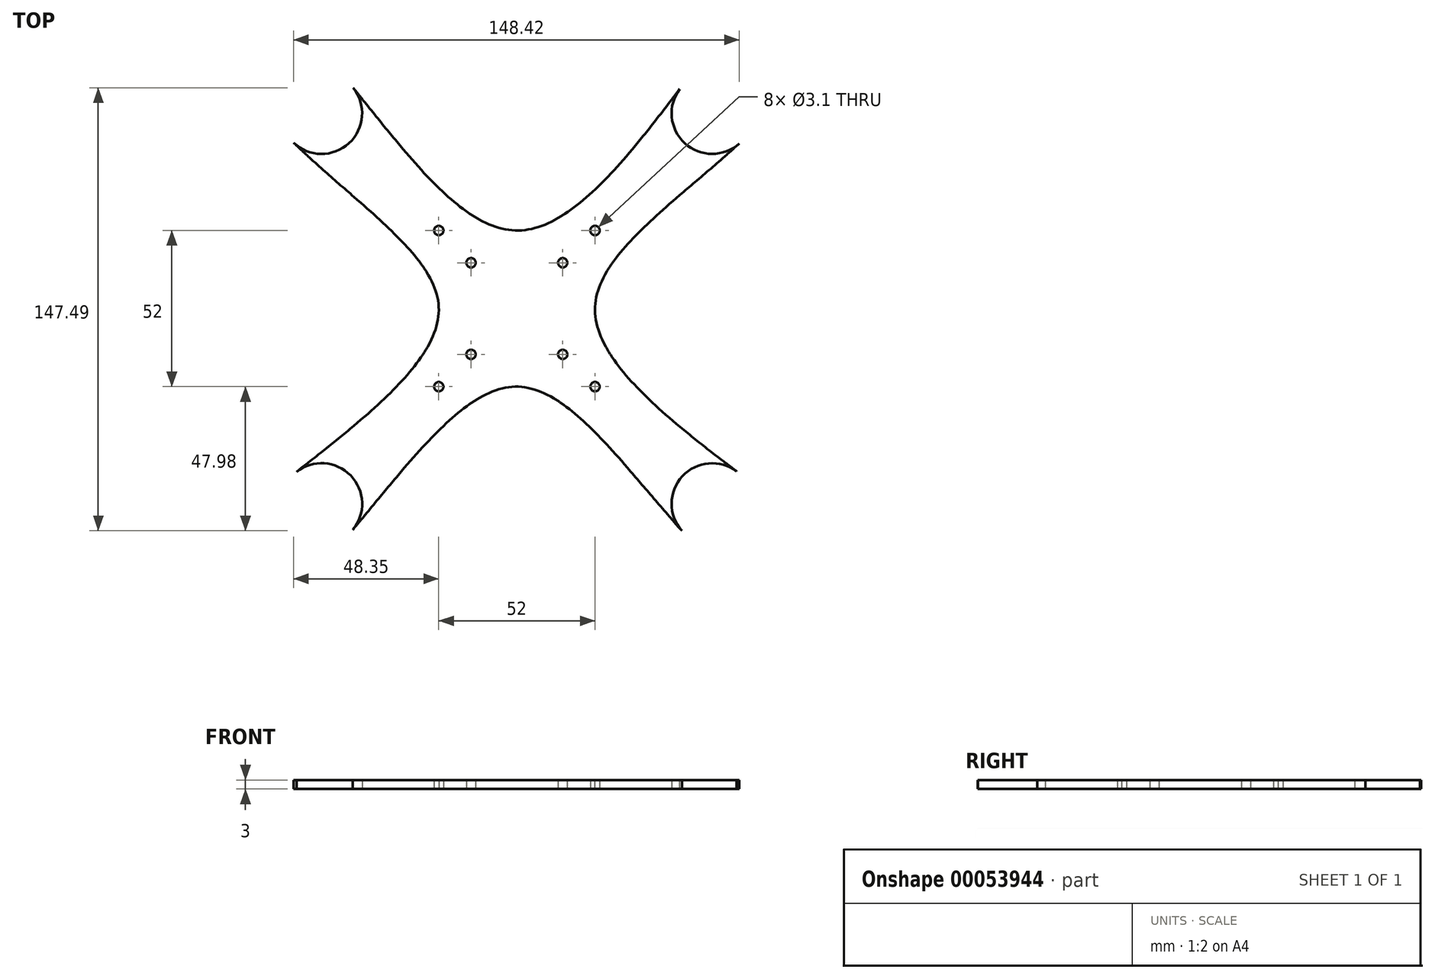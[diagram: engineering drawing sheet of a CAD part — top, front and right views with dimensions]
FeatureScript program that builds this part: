
annotation { "Feature Type Name" : "Feature", "Feature Type Description" : "" }
export const myFeature = defineFeature(function(context is Context, id is Id, definition is map)
    precondition{}
    {
        {
            var Q0;
            Q0=qCreatedBy(makeId("Top.planeOp"),FACE);
            var sketch = newSketch(context, id + "F0", { "sketchPlane" : qUnion([Q0])});
            skLineSegment(sketch, "E0.rect.bottom", {"start": v(-65, -65) * mm, "end": v(65, -65) * mm, "construction": true});
            skLineSegment(sketch, "E0.rect.top", {"start": v(-65, 65) * mm, "end": v(65, 65) * mm, "construction": true});
            skLineSegment(sketch, "E0.rect.left", {"start": v(-65, -65) * mm, "end": v(-65, 65) * mm, "construction": true});
            skLineSegment(sketch, "E0.rect.right", {"start": v(65, -65) * mm, "end": v(65, 65) * mm, "construction": true});
            skPoint(sketch, "E0.rect.middle", {"position": v(0, 0) * mm});
            skCircle(sketch, "E1", {"center": v(-65, 65) * mm, "radius": 50.75 * mm, "construction": true});
            skCircle(sketch, "E2", {"center": v(65, 65) * mm, "radius": 50.75 * mm, "construction": true});
            skCircle(sketch, "E3", {"center": v(65, -65) * mm, "radius": 50.75 * mm, "construction": true});
            skCircle(sketch, "E4", {"center": v(-65, -65) * mm, "radius": 50.75 * mm, "construction": true});
            skArc(sketch, "E5", {"start": v(-77.6, 69.86) * mm, "mid": v(-55.45, 55.45) * mm, "end": v(-69.86, 77.6) * mm});
            skArc(sketch, "E6", {"start": v(69.86, 77.6) * mm, "mid": v(55.45, 55.45) * mm, "end": v(77.6, 69.86) * mm});
            skArc(sketch, "E7", {"start": v(77.6, -69.86) * mm, "mid": v(55.45, -55.45) * mm, "end": v(69.86, -77.6) * mm});
            skArc(sketch, "E8", {"start": v(-69.86, -77.6) * mm, "mid": v(-55.45, -55.45) * mm, "end": v(-77.6, -69.86) * mm});
            skLineSegment(sketch, "E9.rect.bottom", {"start": v(26, -26) * mm, "end": v(-26, -26) * mm, "construction": true});
            skLineSegment(sketch, "E9.rect.top", {"start": v(26, 26) * mm, "end": v(-26, 26) * mm, "construction": true});
            skLineSegment(sketch, "E9.rect.left", {"start": v(26, -26) * mm, "end": v(26, 26) * mm, "construction": true});
            skLineSegment(sketch, "E9.rect.right", {"start": v(-26, -26) * mm, "end": v(-26, 26) * mm, "construction": true});
            skFitSpline(sketch, "E10", {"points": [v(-74.35, 55.26) * mm, v(-26, 0) * mm, v(-73.36, -54.4) * mm], "startDerivative": vector(138.42, -132.82) * mm, "endDerivative": vector(-144.38, -113.88) * mm});
            skFitSpline(sketch, "E11", {"points": [v(74.07, 55) * mm, v(26, 0) * mm, v(73.19, -54.27) * mm], "startDerivative": vector(-139.4, -126.45) * mm, "endDerivative": vector(143.94, -109.76) * mm});
            skFitSpline(sketch, "E12", {"points": [v(54.92, -73.98) * mm, v(0, -26) * mm, v(-54.66, -73.68) * mm], "startDerivative": vector(-126.12, 141.5) * mm, "endDerivative": vector(-120.97, -144.22) * mm});
            skFitSpline(sketch, "E13", {"points": [v(-54.52, 73.5) * mm, v(0, 26) * mm, v(54.26, 73.17) * mm], "startDerivative": vector(114.67, -141.24) * mm, "endDerivative": vector(108.47, 142.58) * mm});
            skLineSegment(sketch, "E14.rect.bottom", {"start": v(-15.25, -15.25) * mm, "end": v(15.25, -15.25) * mm, "construction": true});
            skLineSegment(sketch, "E14.rect.top", {"start": v(-15.25, 15.25) * mm, "end": v(15.25, 15.25) * mm, "construction": true});
            skLineSegment(sketch, "E14.rect.left", {"start": v(-15.25, -15.25) * mm, "end": v(-15.25, 15.25) * mm, "construction": true});
            skLineSegment(sketch, "E14.rect.right", {"start": v(15.25, -15.25) * mm, "end": v(15.25, 15.25) * mm, "construction": true});
            skArc(sketch, "E15", {"start": v(-4.8, 73.17) * mm, "mid": v(-17.28, 102.6) * mm, "end": v(-42.96, 121.6) * mm});
            skArc(sketch, "E16", {"start": v(4.8, 73.17) * mm, "mid": v(17.28, 102.6) * mm, "end": v(42.96, 121.6) * mm});
            skArc(sketch, "E17", {"start": v(73.17, -4.8) * mm, "mid": v(102.6, -17.28) * mm, "end": v(121.6, -42.96) * mm});
            skArc(sketch, "E18", {"start": v(-4.8, -73.17) * mm, "mid": v(-17.28, -102.6) * mm, "end": v(-42.96, -121.6) * mm});
            skArc(sketch, "E19.0", {"start": v(-4.6, 90.96) * mm, "mid": v(-19.8, 112.75) * mm, "end": v(-42.39, 126.74) * mm});
            skArc(sketch, "E20.0", {"start": v(4.6, 90.96) * mm, "mid": v(19.8, 112.75) * mm, "end": v(42.39, 126.74) * mm});
            skLineSegment(sketch, "E21.0.left", {"start": v(-47.27, 67.5) * mm, "end": v(-9.76, 67.5) * mm});
            skLineSegment(sketch, "E22.1.right", {"start": v(-47.17, -67.5) * mm, "end": v(-9.76, -67.5) * mm});
            skLineSegment(sketch, "E23.0.right", {"start": v(67.5, -47.45) * mm, "end": v(67.5, -9.76) * mm});
            skArc(sketch, "E24.trimOffspring", {"start": v(-4.6, -90.96) * mm, "mid": v(-19.8, -112.75) * mm, "end": v(-42.39, -126.74) * mm});
            skArc(sketch, "E25.trimOffspring", {"start": v(90.96, -4.6) * mm, "mid": v(112.75, -19.8) * mm, "end": v(126.74, -42.39) * mm});
            skLineSegment(sketch, "E26.trimOffspring", {"start": v(-35.06, 62.5) * mm, "end": v(35.61, 62.5) * mm});
            skLineSegment(sketch, "E27.trimOffspring", {"start": v(-62.5, -35.22) * mm, "end": v(-62.5, 33.4) * mm});
            skLineSegment(sketch, "E28.trimOffspring", {"start": v(-67.5, -47.35) * mm, "end": v(-67.5, -9.76) * mm});
            skLineSegment(sketch, "E29.trimOffspring", {"start": v(-34.67, -62.5) * mm, "end": v(34.1, -62.5) * mm});
            skLineSegment(sketch, "E30.trimOffspring", {"start": v(62.5, -35.55) * mm, "end": v(62.5, 34) * mm});
            skPoint(sketch, "E31.visualSharp", {"position": v(-74.9, 0) * mm});
            skArc(sketch, "E31.filletArc", {"start": v(-90.96, -4.6) * mm, "mid": v(-87.94, 0) * mm, "end": v(-90.96, 4.6) * mm});
            skPoint(sketch, "E32.visualSharp", {"position": v(0, 74.9) * mm});
            skArc(sketch, "E32.filletArc", {"start": v(-4.6, 90.96) * mm, "mid": v(0, 87.94) * mm, "end": v(4.6, 90.96) * mm});
            skPoint(sketch, "E33.visualSharp", {"position": v(74.9, 0) * mm});
            skArc(sketch, "E33.filletArc", {"start": v(90.96, 4.6) * mm, "mid": v(87.94, 0) * mm, "end": v(90.96, -4.6) * mm});
            skPoint(sketch, "E34.visualSharp", {"position": v(0, -74.9) * mm});
            skArc(sketch, "E34.filletArc", {"start": v(4.6, -90.96) * mm, "mid": v(0, -87.94) * mm, "end": v(-4.6, -90.96) * mm});
            skLineSegment(sketch, "E35.trimOffspring", {"start": v(9.76, 67.5) * mm, "end": v(47.45, 67.5) * mm});
            skLineSegment(sketch, "E36.trimOffspring", {"start": v(67.5, 9.76) * mm, "end": v(67.5, 46.9) * mm});
            skLineSegment(sketch, "E37.trimOffspring", {"start": v(-67.5, 9.76) * mm, "end": v(-67.5, 46.68) * mm});
            skLineSegment(sketch, "E38.trimOffspring", {"start": v(9.76, -67.5) * mm, "end": v(46.96, -67.5) * mm});
            skPoint(sketch, "E39.visualSharp", {"position": v(67.5, 4.3) * mm});
            skArc(sketch, "E39.filletArc", {"start": v(67.5, 9.76) * mm, "mid": v(69.21, 6) * mm, "end": v(73.17, 4.8) * mm});
            skPoint(sketch, "E40.visualSharp", {"position": v(67.5, -4.3) * mm});
            skArc(sketch, "E40.filletArc", {"start": v(73.17, -4.8) * mm, "mid": v(69.21, -6) * mm, "end": v(67.5, -9.76) * mm});
            skPoint(sketch, "E41.visualSharp", {"position": v(4.3, 67.5) * mm});
            skArc(sketch, "E41.filletArc", {"start": v(4.8, 73.17) * mm, "mid": v(6, 69.21) * mm, "end": v(9.76, 67.5) * mm});
            skPoint(sketch, "E42.visualSharp", {"position": v(-4.3, 67.5) * mm});
            skArc(sketch, "E42.filletArc", {"start": v(-9.76, 67.5) * mm, "mid": v(-6, 69.21) * mm, "end": v(-4.8, 73.17) * mm});
            skPoint(sketch, "E43.visualSharp", {"position": v(-67.5, 4.3) * mm});
            skArc(sketch, "E43.filletArc", {"start": v(-73.17, 4.8) * mm, "mid": v(-69.21, 6) * mm, "end": v(-67.5, 9.76) * mm});
            skPoint(sketch, "E44.visualSharp", {"position": v(-67.5, -4.3) * mm});
            skArc(sketch, "E44.filletArc", {"start": v(-67.5, -9.76) * mm, "mid": v(-69.21, -6) * mm, "end": v(-73.17, -4.8) * mm});
            skPoint(sketch, "E45.visualSharp", {"position": v(-4.3, -67.5) * mm});
            skArc(sketch, "E45.filletArc", {"start": v(-4.8, -73.17) * mm, "mid": v(-6, -69.21) * mm, "end": v(-9.76, -67.5) * mm});
            skPoint(sketch, "E46.visualSharp", {"position": v(4.3, -67.5) * mm});
            skArc(sketch, "E46.filletArc", {"start": v(9.76, -67.5) * mm, "mid": v(6, -69.21) * mm, "end": v(4.8, -73.17) * mm});
            skFitSpline(sketch, "E47.trimOffspring", {"points": [v(74.07, 55) * mm, v(26, 0) * mm, v(73.19, -54.27) * mm], "startDerivative": vector(-139.4, -126.45) * mm, "endDerivative": vector(143.94, -109.76) * mm});
            skPoint(sketch, "E48.visualSharp", {"position": v(46.05, 62.5) * mm});
            skArc(sketch, "E48.filletArc", {"start": v(39.46, 54.3) * mm, "mid": v(40.14, 59.63) * mm, "end": v(35.61, 62.5) * mm});
            skPoint(sketch, "E49.visualSharp", {"position": v(-45.64, 62.5) * mm});
            skArc(sketch, "E49.filletArc", {"start": v(-35.06, 62.5) * mm, "mid": v(-39.6, 59.61) * mm, "end": v(-38.89, 54.28) * mm});
            skFitSpline(sketch, "E50.trimOffspring", {"points": [v(74.07, 55) * mm, v(26, 0) * mm, v(73.19, -54.27) * mm], "startDerivative": vector(-139.4, -126.45) * mm, "endDerivative": vector(143.94, -109.76) * mm});
            skPoint(sketch, "E51.visualSharp", {"position": v(-62.5, 44.43) * mm});
            skArc(sketch, "E51.filletArc", {"start": v(-54.2, 37.17) * mm, "mid": v(-59.57, 37.96) * mm, "end": v(-62.5, 33.4) * mm});
            skPoint(sketch, "E52.visualSharp", {"position": v(-62.5, -45.8) * mm});
            skArc(sketch, "E52.filletArc", {"start": v(-62.5, -35.22) * mm, "mid": v(-59.6, -39.76) * mm, "end": v(-54.28, -39.05) * mm});
            skPoint(sketch, "E53.visualSharp", {"position": v(-45.38, -62.5) * mm});
            skArc(sketch, "E53.filletArc", {"start": v(-38.48, -54.26) * mm, "mid": v(-39.21, -59.6) * mm, "end": v(-34.67, -62.5) * mm});
            skPoint(sketch, "E54.visualSharp", {"position": v(44.96, -62.5) * mm});
            skArc(sketch, "E54.filletArc", {"start": v(34.1, -62.5) * mm, "mid": v(38.64, -59.58) * mm, "end": v(37.88, -54.23) * mm});
            skPoint(sketch, "E55.visualSharp", {"position": v(62.5, -46.02) * mm});
            skArc(sketch, "E55.filletArc", {"start": v(54.3, -39.4) * mm, "mid": v(59.62, -40.08) * mm, "end": v(62.5, -35.55) * mm});
            skPoint(sketch, "E56.visualSharp", {"position": v(62.5, 44.86) * mm});
            skArc(sketch, "E56.filletArc", {"start": v(62.5, 34) * mm, "mid": v(59.58, 38.54) * mm, "end": v(54.24, 37.78) * mm});
            skPoint(sketch, "E57.visualSharp", {"position": v(67.5, 49.17) * mm});
            skArc(sketch, "E57.filletArc", {"start": v(69.2, 50.66) * mm, "mid": v(67.95, 48.96) * mm, "end": v(67.5, 46.9) * mm});
            skPoint(sketch, "E58.visualSharp", {"position": v(49.92, 67.5) * mm});
            skArc(sketch, "E58.filletArc", {"start": v(47.45, 67.5) * mm, "mid": v(49.67, 68.02) * mm, "end": v(51.43, 69.46) * mm});
            skPoint(sketch, "E59.visualSharp", {"position": v(-49.67, 67.5) * mm});
            skArc(sketch, "E59.filletArc", {"start": v(-51.17, 69.36) * mm, "mid": v(-49.43, 67.99) * mm, "end": v(-47.27, 67.5) * mm});
            skPoint(sketch, "E60.visualSharp", {"position": v(-67.5, 48.9) * mm});
            skArc(sketch, "E60.filletArc", {"start": v(-67.5, 46.68) * mm, "mid": v(-67.92, 48.7) * mm, "end": v(-69.12, 50.37) * mm});
            skPoint(sketch, "E61.visualSharp", {"position": v(-67.5, -49.77) * mm});
            skArc(sketch, "E61.filletArc", {"start": v(-69.4, -51.28) * mm, "mid": v(-68, -49.53) * mm, "end": v(-67.5, -47.35) * mm});
            skPoint(sketch, "E62.visualSharp", {"position": v(-49.52, -67.5) * mm});
            skArc(sketch, "E62.filletArc", {"start": v(-47.17, -67.5) * mm, "mid": v(-49.3, -67.97) * mm, "end": v(-51.02, -69.3) * mm});
            skPoint(sketch, "E63.visualSharp", {"position": v(49.25, -67.5) * mm});
            skArc(sketch, "E63.filletArc", {"start": v(50.74, -69.22) * mm, "mid": v(49.04, -67.95) * mm, "end": v(46.96, -67.5) * mm});
            skPoint(sketch, "E64.visualSharp", {"position": v(67.5, -49.9) * mm});
            skArc(sketch, "E64.filletArc", {"start": v(67.5, -47.45) * mm, "mid": v(68.02, -49.66) * mm, "end": v(69.46, -51.41) * mm});
            skLineSegment(sketch, "E65", {"start": v(-65, 65) * mm, "end": v(-111.5, 111.5) * mm, "construction": true});
            skLineSegment(sketch, "E66", {"start": v(65, 65) * mm, "end": v(111.5, 111.5) * mm, "construction": true});
            skLineSegment(sketch, "E67", {"start": v(65, -65) * mm, "end": v(111.5, -111.5) * mm, "construction": true});
            skLineSegment(sketch, "E68", {"start": v(-65, -65) * mm, "end": v(-111.5, -111.5) * mm, "construction": true});
            skLineSegment(sketch, "E69.0.left", {"start": v(-78.73, 75.2) * mm, "end": v(-105.83, 102.3) * mm});
            skLineSegment(sketch, "E69.0.right", {"start": v(-75.2, 78.73) * mm, "end": v(-102.3, 105.83) * mm});
            skLineSegment(sketch, "E69.1.left", {"start": v(75.2, 78.73) * mm, "end": v(102.3, 105.83) * mm});
            skLineSegment(sketch, "E69.1.right", {"start": v(78.73, 75.2) * mm, "end": v(105.83, 102.3) * mm});
            skLineSegment(sketch, "E69.2.left", {"start": v(78.73, -75.2) * mm, "end": v(105.83, -102.3) * mm});
            skLineSegment(sketch, "E69.2.right", {"start": v(75.2, -78.73) * mm, "end": v(102.3, -105.83) * mm});
            skLineSegment(sketch, "E69.3.left", {"start": v(-75.2, -78.73) * mm, "end": v(-102.3, -105.83) * mm});
            skLineSegment(sketch, "E69.3.right", {"start": v(-78.73, -75.2) * mm, "end": v(-105.83, -102.3) * mm});
            skLineSegment(sketch, "E70.trimOffspring", {"start": v(-113.23, 109.7) * mm, "end": v(-113.26, 109.72) * mm});
            skLineSegment(sketch, "E71.trimOffspring", {"start": v(-109.7, 113.23) * mm, "end": v(-109.72, 113.26) * mm});
            skArc(sketch, "E72.trimOffspring", {"start": v(-113.35, 101.79) * mm, "mid": v(-123.85, 80.08) * mm, "end": v(-125.08, 56) * mm});
            skLineSegment(sketch, "E73.trimOffspring", {"start": v(113.23, 109.7) * mm, "end": v(113.26, 109.72) * mm});
            skLineSegment(sketch, "E74.trimOffspring", {"start": v(109.7, 113.23) * mm, "end": v(109.72, 113.26) * mm});
            skArc(sketch, "E75.trimOffspring", {"start": v(113.35, 101.79) * mm, "mid": v(123.85, 80.08) * mm, "end": v(125.08, 56) * mm});
            skLineSegment(sketch, "E76.trimOffspring", {"start": v(113.23, -109.7) * mm, "end": v(113.26, -109.72) * mm});
            skLineSegment(sketch, "E77.trimOffspring", {"start": v(109.7, -113.23) * mm, "end": v(109.72, -113.26) * mm});
            skArc(sketch, "E78.trimOffspring", {"start": v(101.79, -113.35) * mm, "mid": v(80.08, -123.85) * mm, "end": v(56, -125.08) * mm});
            skArc(sketch, "E79.trimOffspring", {"start": v(-113.35, -101.79) * mm, "mid": v(-123.85, -80.08) * mm, "end": v(-125.08, -56) * mm});
            skLineSegment(sketch, "E80.trimOffspring", {"start": v(-113.23, -109.7) * mm, "end": v(-113.26, -109.72) * mm});
            skLineSegment(sketch, "E81.trimOffspring", {"start": v(-109.7, -113.23) * mm, "end": v(-109.72, -113.26) * mm});
            skPoint(sketch, "E82.visualSharp", {"position": v(106.15, 109.69) * mm});
            skArc(sketch, "E82.filletArc", {"start": v(102.3, 105.83) * mm, "mid": v(103.75, 109.7) * mm, "end": v(101.79, 113.35) * mm});
            skPoint(sketch, "E83.visualSharp", {"position": v(109.69, 106.15) * mm});
            skArc(sketch, "E83.filletArc", {"start": v(113.35, 101.79) * mm, "mid": v(109.7, 103.75) * mm, "end": v(105.83, 102.3) * mm});
            skPoint(sketch, "E84.visualSharp", {"position": v(76.15, 72.61) * mm});
            skArc(sketch, "E84.filletArc", {"start": v(78.73, 75.2) * mm, "mid": v(77.37, 72.7) * mm, "end": v(77.6, 69.86) * mm});
            skPoint(sketch, "E85.visualSharp", {"position": v(72.61, 76.15) * mm});
            skArc(sketch, "E85.filletArc", {"start": v(69.86, 77.6) * mm, "mid": v(72.7, 77.37) * mm, "end": v(75.2, 78.73) * mm});
            skPoint(sketch, "E86.visualSharp", {"position": v(-72.61, 76.15) * mm});
            skArc(sketch, "E86.filletArc", {"start": v(-75.2, 78.73) * mm, "mid": v(-72.7, 77.37) * mm, "end": v(-69.86, 77.6) * mm});
            skPoint(sketch, "E87.visualSharp", {"position": v(-76.15, 72.61) * mm});
            skArc(sketch, "E87.filletArc", {"start": v(-77.6, 69.86) * mm, "mid": v(-77.37, 72.7) * mm, "end": v(-78.73, 75.2) * mm});
            skPoint(sketch, "E88.visualSharp", {"position": v(-106.15, 109.69) * mm});
            skArc(sketch, "E88.filletArc", {"start": v(-101.79, 113.35) * mm, "mid": v(-103.75, 109.7) * mm, "end": v(-102.3, 105.83) * mm});
            skPoint(sketch, "E89.visualSharp", {"position": v(-109.69, 106.15) * mm});
            skArc(sketch, "E89.filletArc", {"start": v(-105.83, 102.3) * mm, "mid": v(-109.7, 103.75) * mm, "end": v(-113.35, 101.79) * mm});
            skPoint(sketch, "E90.visualSharp", {"position": v(76.15, -72.61) * mm});
            skArc(sketch, "E90.filletArc", {"start": v(77.6, -69.86) * mm, "mid": v(77.37, -72.7) * mm, "end": v(78.73, -75.2) * mm});
            skPoint(sketch, "E91.visualSharp", {"position": v(109.69, -106.15) * mm});
            skArc(sketch, "E91.filletArc", {"start": v(105.83, -102.3) * mm, "mid": v(109.7, -103.75) * mm, "end": v(113.35, -101.79) * mm});
            skPoint(sketch, "E92.visualSharp", {"position": v(106.15, -109.69) * mm});
            skArc(sketch, "E92.filletArc", {"start": v(101.79, -113.35) * mm, "mid": v(103.75, -109.7) * mm, "end": v(102.3, -105.83) * mm});
            skPoint(sketch, "E93.visualSharp", {"position": v(72.61, -76.15) * mm});
            skArc(sketch, "E93.filletArc", {"start": v(75.2, -78.73) * mm, "mid": v(72.7, -77.37) * mm, "end": v(69.86, -77.6) * mm});
            skPoint(sketch, "E94.visualSharp", {"position": v(-72.61, -76.15) * mm});
            skArc(sketch, "E94.filletArc", {"start": v(-69.86, -77.6) * mm, "mid": v(-72.7, -77.37) * mm, "end": v(-75.2, -78.73) * mm});
            skPoint(sketch, "E95.visualSharp", {"position": v(-76.15, -72.61) * mm});
            skArc(sketch, "E95.filletArc", {"start": v(-78.73, -75.2) * mm, "mid": v(-77.37, -72.7) * mm, "end": v(-77.6, -69.86) * mm});
            skPoint(sketch, "E96.visualSharp", {"position": v(-106.15, -109.69) * mm});
            skArc(sketch, "E96.filletArc", {"start": v(-102.3, -105.83) * mm, "mid": v(-103.75, -109.7) * mm, "end": v(-101.79, -113.35) * mm});
            skPoint(sketch, "E97.visualSharp", {"position": v(-109.69, -106.15) * mm});
            skArc(sketch, "E97.filletArc", {"start": v(-113.35, -101.79) * mm, "mid": v(-109.7, -103.75) * mm, "end": v(-105.83, -102.3) * mm});
            skCircle(sketch, "E98", {"center": v(-15.25, 15.25) * mm, "radius": 1.55 * mm});
            skCircle(sketch, "E99", {"center": v(15.25, 15.25) * mm, "radius": 1.55 * mm});
            skCircle(sketch, "E100", {"center": v(15.25, -15.25) * mm, "radius": 1.55 * mm});
            skCircle(sketch, "E101", {"center": v(-15.25, -15.25) * mm, "radius": 1.55 * mm});
            skCircle(sketch, "E102", {"center": v(-65, 65) * mm, "radius": 4.5 * mm});
            skCircle(sketch, "E103", {"center": v(65, 65) * mm, "radius": 4.5 * mm});
            skCircle(sketch, "E104", {"center": v(65, -65) * mm, "radius": 4.5 * mm});
            skCircle(sketch, "E105", {"center": v(-65, -65) * mm, "radius": 4.5 * mm});
            skCircle(sketch, "E106", {"center": v(-26, 26) * mm, "radius": 1.55 * mm});
            skCircle(sketch, "E107", {"center": v(26, 26) * mm, "radius": 1.55 * mm});
            skCircle(sketch, "E108", {"center": v(-26, -26) * mm, "radius": 1.55 * mm});
            skCircle(sketch, "E109", {"center": v(26, -26) * mm, "radius": 1.55 * mm});
            skLineSegment(sketch, "E110", {"start": v(65, 57) * mm, "end": v(65, 55.5) * mm});
            skLineSegment(sketch, "E111", {"start": v(57, 65) * mm, "end": v(55.5, 65) * mm});
            skLineSegment(sketch, "E112", {"start": v(73, 65) * mm, "end": v(74.5, 65) * mm});
            skLineSegment(sketch, "E113", {"start": v(65, 73) * mm, "end": v(65, 74.5) * mm});
            skArc(sketch, "E114.0.startCap", {"start": v(73, 63.5) * mm, "mid": v(71.5, 65) * mm, "end": v(73, 66.5) * mm});
            skArc(sketch, "E114.0.endCap", {"start": v(74.5, 66.5) * mm, "mid": v(76, 65) * mm, "end": v(74.5, 63.5) * mm});
            skLineSegment(sketch, "E114.0.left", {"start": v(73, 66.5) * mm, "end": v(74.5, 66.5) * mm});
            skLineSegment(sketch, "E114.0.right", {"start": v(73, 63.5) * mm, "end": v(74.5, 63.5) * mm});
            skArc(sketch, "E115.0.startCap", {"start": v(66.5, 73) * mm, "mid": v(65, 71.5) * mm, "end": v(63.5, 73) * mm});
            skArc(sketch, "E115.0.endCap", {"start": v(63.5, 74.5) * mm, "mid": v(65, 76) * mm, "end": v(66.5, 74.5) * mm});
            skLineSegment(sketch, "E115.0.left", {"start": v(63.5, 73) * mm, "end": v(63.5, 74.5) * mm});
            skLineSegment(sketch, "E115.0.right", {"start": v(66.5, 73) * mm, "end": v(66.5, 74.5) * mm});
            skArc(sketch, "E116.0.startCap", {"start": v(57, 66.5) * mm, "mid": v(58.5, 65) * mm, "end": v(57, 63.5) * mm});
            skArc(sketch, "E116.0.endCap", {"start": v(55.5, 63.5) * mm, "mid": v(54, 65) * mm, "end": v(55.5, 66.5) * mm});
            skLineSegment(sketch, "E116.0.left", {"start": v(57, 63.5) * mm, "end": v(55.5, 63.5) * mm});
            skLineSegment(sketch, "E116.0.right", {"start": v(57, 66.5) * mm, "end": v(55.5, 66.5) * mm});
            skArc(sketch, "E117.0.startCap", {"start": v(63.5, 57) * mm, "mid": v(65, 58.5) * mm, "end": v(66.5, 57) * mm});
            skArc(sketch, "E117.0.endCap", {"start": v(66.5, 55.5) * mm, "mid": v(65, 54) * mm, "end": v(63.5, 55.5) * mm});
            skLineSegment(sketch, "E117.0.left", {"start": v(66.5, 57) * mm, "end": v(66.5, 55.5) * mm});
            skLineSegment(sketch, "E117.0.right", {"start": v(63.5, 57) * mm, "end": v(63.5, 55.5) * mm});
            skLineSegment(sketch, "E118", {"start": v(0, 153.86) * mm, "end": v(0, -113.26) * mm, "construction": true});
            skArc(sketch, "E119.MirrorCS", {"start": v(-66.5, 55.5) * mm, "mid": v(-65, 54) * mm, "end": v(-63.5, 55.5) * mm});
            skLineSegment(sketch, "E120.MirrorCS", {"start": v(-66.5, 57) * mm, "end": v(-66.5, 55.5) * mm});
            skLineSegment(sketch, "E121.MirrorCS", {"start": v(-63.5, 57) * mm, "end": v(-63.5, 55.5) * mm});
            skArc(sketch, "E122.MirrorCS", {"start": v(-63.5, 57) * mm, "mid": v(-65, 58.5) * mm, "end": v(-66.5, 57) * mm});
            skLineSegment(sketch, "E123.MirrorCS", {"start": v(-65, 57) * mm, "end": v(-65, 55.5) * mm});
            skArc(sketch, "E124.MirrorCS", {"start": v(-73, 63.5) * mm, "mid": v(-71.5, 65) * mm, "end": v(-73, 66.5) * mm});
            skLineSegment(sketch, "E125.MirrorCS", {"start": v(-73, 63.5) * mm, "end": v(-74.5, 63.5) * mm});
            skLineSegment(sketch, "E126.MirrorCS", {"start": v(-73, 66.5) * mm, "end": v(-74.5, 66.5) * mm});
            skLineSegment(sketch, "E127.MirrorCS", {"start": v(-73, 65) * mm, "end": v(-74.5, 65) * mm});
            skArc(sketch, "E128.MirrorCS", {"start": v(-74.5, 66.5) * mm, "mid": v(-76, 65) * mm, "end": v(-74.5, 63.5) * mm});
            skLineSegment(sketch, "E129.MirrorCS", {"start": v(-57, 63.5) * mm, "end": v(-55.5, 63.5) * mm});
            skArc(sketch, "E130.MirrorCS", {"start": v(-55.5, 63.5) * mm, "mid": v(-54, 65) * mm, "end": v(-55.5, 66.5) * mm});
            skLineSegment(sketch, "E131.MirrorCS", {"start": v(-66.5, 73) * mm, "end": v(-66.5, 74.5) * mm});
            skLineSegment(sketch, "E132.MirrorCS", {"start": v(-57, 66.5) * mm, "end": v(-55.5, 66.5) * mm});
            skArc(sketch, "E133.MirrorCS", {"start": v(-57, 66.5) * mm, "mid": v(-58.5, 65) * mm, "end": v(-57, 63.5) * mm});
            skArc(sketch, "E134.MirrorCS", {"start": v(-63.5, 74.5) * mm, "mid": v(-65, 76) * mm, "end": v(-66.5, 74.5) * mm});
            skArc(sketch, "E135.MirrorCS", {"start": v(-66.5, 73) * mm, "mid": v(-65, 71.5) * mm, "end": v(-63.5, 73) * mm});
            skLineSegment(sketch, "E136", {"start": v(-63.5, 74.5) * mm, "end": v(-63.5, 73) * mm});
            skLineSegment(sketch, "E137", {"start": v(125.68, 0) * mm, "end": v(-117.28, 0) * mm, "construction": true});
            skArc(sketch, "E138.MirrorCS", {"start": v(-66.5, -55.5) * mm, "mid": v(-65, -54) * mm, "end": v(-63.5, -55.5) * mm});
            skLineSegment(sketch, "E139.MirrorCS", {"start": v(-63.5, -57) * mm, "end": v(-63.5, -55.5) * mm});
            skLineSegment(sketch, "E140.MirrorCS", {"start": v(-66.5, -57) * mm, "end": v(-66.5, -55.5) * mm});
            skLineSegment(sketch, "E141.MirrorCS", {"start": v(-65, -57) * mm, "end": v(-65, -55.5) * mm});
            skArc(sketch, "E142.MirrorCS", {"start": v(-63.5, -57) * mm, "mid": v(-65, -58.5) * mm, "end": v(-66.5, -57) * mm});
            skArc(sketch, "E143.MirrorCS", {"start": v(-74.5, -66.5) * mm, "mid": v(-76, -65) * mm, "end": v(-74.5, -63.5) * mm});
            skLineSegment(sketch, "E144.MirrorCS", {"start": v(-73, -65) * mm, "end": v(-74.5, -65) * mm});
            skLineSegment(sketch, "E145.MirrorCS", {"start": v(-73, -66.5) * mm, "end": v(-74.5, -66.5) * mm});
            skLineSegment(sketch, "E146.MirrorCS", {"start": v(-73, -63.5) * mm, "end": v(-74.5, -63.5) * mm});
            skArc(sketch, "E147.MirrorCS", {"start": v(-73, -63.5) * mm, "mid": v(-71.5, -65) * mm, "end": v(-73, -66.5) * mm});
            skLineSegment(sketch, "E148.MirrorCS", {"start": v(-57, -63.5) * mm, "end": v(-55.5, -63.5) * mm});
            skLineSegment(sketch, "E149.MirrorCS", {"start": v(-57, -66.5) * mm, "end": v(-55.5, -66.5) * mm});
            skArc(sketch, "E150.MirrorCS", {"start": v(-57, -66.5) * mm, "mid": v(-58.5, -65) * mm, "end": v(-57, -63.5) * mm});
            skArc(sketch, "E151.MirrorCS", {"start": v(-55.5, -63.5) * mm, "mid": v(-54, -65) * mm, "end": v(-55.5, -66.5) * mm});
            skArc(sketch, "E152.MirrorCS", {"start": v(-66.5, -73) * mm, "mid": v(-65, -71.5) * mm, "end": v(-63.5, -73) * mm});
            skArc(sketch, "E153.MirrorCS", {"start": v(-63.5, -74.5) * mm, "mid": v(-65, -76) * mm, "end": v(-66.5, -74.5) * mm});
            skLineSegment(sketch, "E154.MirrorCS", {"start": v(-66.5, -73) * mm, "end": v(-66.5, -74.5) * mm});
            skLineSegment(sketch, "E155.MirrorCS", {"start": v(-63.5, -74.5) * mm, "end": v(-63.5, -73) * mm});
            skLineSegment(sketch, "E156.MirrorCS", {"start": v(65, -57) * mm, "end": v(65, -55.5) * mm});
            skLineSegment(sketch, "E157.MirrorCS", {"start": v(63.5, -57) * mm, "end": v(63.5, -55.5) * mm});
            skLineSegment(sketch, "E158.MirrorCS", {"start": v(66.5, -57) * mm, "end": v(66.5, -55.5) * mm});
            skArc(sketch, "E159.MirrorCS", {"start": v(66.5, -55.5) * mm, "mid": v(65, -54) * mm, "end": v(63.5, -55.5) * mm});
            skArc(sketch, "E160.MirrorCS", {"start": v(63.5, -57) * mm, "mid": v(65, -58.5) * mm, "end": v(66.5, -57) * mm});
            skArc(sketch, "E161.MirrorCS", {"start": v(74.5, -66.5) * mm, "mid": v(76, -65) * mm, "end": v(74.5, -63.5) * mm});
            skLineSegment(sketch, "E162.MirrorCS", {"start": v(73, -65) * mm, "end": v(74.5, -65) * mm});
            skLineSegment(sketch, "E163.MirrorCS", {"start": v(73, -63.5) * mm, "end": v(74.5, -63.5) * mm});
            skArc(sketch, "E164.MirrorCS", {"start": v(73, -63.5) * mm, "mid": v(71.5, -65) * mm, "end": v(73, -66.5) * mm});
            skLineSegment(sketch, "E165.MirrorCS", {"start": v(73, -66.5) * mm, "end": v(74.5, -66.5) * mm});
            skLineSegment(sketch, "E166.MirrorCS", {"start": v(57, -66.5) * mm, "end": v(55.5, -66.5) * mm});
            skLineSegment(sketch, "E167.MirrorCS", {"start": v(57, -63.5) * mm, "end": v(55.5, -63.5) * mm});
            skArc(sketch, "E168.MirrorCS", {"start": v(55.5, -63.5) * mm, "mid": v(54, -65) * mm, "end": v(55.5, -66.5) * mm});
            skLineSegment(sketch, "E169.MirrorCS", {"start": v(57, -65) * mm, "end": v(55.5, -65) * mm});
            skArc(sketch, "E170.MirrorCS", {"start": v(57, -66.5) * mm, "mid": v(58.5, -65) * mm, "end": v(57, -63.5) * mm});
            skArc(sketch, "E171.MirrorCS", {"start": v(63.5, -74.5) * mm, "mid": v(65, -76) * mm, "end": v(66.5, -74.5) * mm});
            skLineSegment(sketch, "E172.MirrorCS", {"start": v(65, -73) * mm, "end": v(65, -74.5) * mm});
            skLineSegment(sketch, "E173.MirrorCS", {"start": v(63.5, -73) * mm, "end": v(63.5, -74.5) * mm});
            skLineSegment(sketch, "E174.MirrorCS", {"start": v(66.5, -73) * mm, "end": v(66.5, -74.5) * mm});
            skArc(sketch, "E175.MirrorCS", {"start": v(66.5, -73) * mm, "mid": v(65, -71.5) * mm, "end": v(63.5, -73) * mm});
            skArc(sketch, "E176", {"start": v(-122.17, 48.12) * mm, "mid": v(-122.26, 49.77) * mm, "end": v(-123, 51.24) * mm});
            skArc(sketch, "E177.MirrorC", {"start": v(-46.45, 122.85) * mm, "mid": v(-49.77, 122.26) * mm, "end": v(-52.36, 124.42) * mm});
            skArc(sketch, "E178.MirrorC", {"start": v(-130, 49.75) * mm, "mid": v(-129.99, 47.71) * mm, "end": v(-128.98, 45.94) * mm});
            skArc(sketch, "E179.MirrorC", {"start": v(-48.12, 122.17) * mm, "mid": v(-49.77, 122.26) * mm, "end": v(-51.24, 123) * mm});
            skArc(sketch, "E180.MirrorC", {"start": v(130, 49.75) * mm, "mid": v(129.99, 47.71) * mm, "end": v(128.98, 45.94) * mm});
            skArc(sketch, "E181.MirrorC", {"start": v(48.12, 122.17) * mm, "mid": v(49.77, 122.26) * mm, "end": v(51.24, 123) * mm});
            skArc(sketch, "E182.MirrorC", {"start": v(122.17, -48.12) * mm, "mid": v(122.26, -49.77) * mm, "end": v(123, -51.24) * mm});
            skArc(sketch, "E183.MirrorC", {"start": v(49.75, -130) * mm, "mid": v(47.71, -129.99) * mm, "end": v(45.94, -128.98) * mm});
            skArc(sketch, "E184.MirrorC", {"start": v(-48.12, -122.17) * mm, "mid": v(-49.77, -122.26) * mm, "end": v(-51.24, -123) * mm});
            skArc(sketch, "E185.MirrorC", {"start": v(-122.17, -48.12) * mm, "mid": v(-122.26, -49.77) * mm, "end": v(-123, -51.24) * mm});
            skArc(sketch, "E186.trimOffspring", {"start": v(-126.74, 42.39) * mm, "mid": v(-112.75, 19.8) * mm, "end": v(-90.96, 4.6) * mm});
            skArc(sketch, "E187.trimOffspring", {"start": v(-121.6, 42.96) * mm, "mid": v(-102.6, 17.28) * mm, "end": v(-73.17, 4.8) * mm});
            skArc(sketch, "E188.trimOffspring", {"start": v(-122.85, 46.45) * mm, "mid": v(-122.26, 49.77) * mm, "end": v(-124.42, 52.36) * mm});
            skArc(sketch, "E189.trimOffspring", {"start": v(-129.28, 51.2) * mm, "mid": v(-129.99, 47.71) * mm, "end": v(-127.65, 45.04) * mm});
            skArc(sketch, "E190.trimOffspring", {"start": v(-53.95, 129.81) * mm, "mid": v(-111.5, 111.5) * mm, "end": v(-129.81, 53.95) * mm});
            skArc(sketch, "E191.trimOffspring", {"start": v(-56, 125.08) * mm, "mid": v(-80.08, 123.85) * mm, "end": v(-101.79, 113.35) * mm});
            skArc(sketch, "E192.trimOffspring", {"start": v(-51.2, 129.28) * mm, "mid": v(-47.71, 129.99) * mm, "end": v(-45.04, 127.65) * mm});
            skArc(sketch, "E193.trimOffspring", {"start": v(-49.75, 130) * mm, "mid": v(-47.71, 129.99) * mm, "end": v(-45.94, 128.98) * mm});
            skArc(sketch, "E194.trimOffspring", {"start": v(49.75, 130) * mm, "mid": v(47.71, 129.99) * mm, "end": v(45.94, 128.98) * mm});
            skArc(sketch, "E195.trimOffspring", {"start": v(53.95, 129.81) * mm, "mid": v(111.5, 111.5) * mm, "end": v(129.81, 53.95) * mm});
            skArc(sketch, "E196.trimOffspring", {"start": v(56, 125.08) * mm, "mid": v(80.08, 123.85) * mm, "end": v(101.79, 113.35) * mm});
            skArc(sketch, "E197.trimOffspring", {"start": v(121.6, 42.96) * mm, "mid": v(102.6, 17.28) * mm, "end": v(73.17, 4.8) * mm});
            skArc(sketch, "E198.trimOffspring", {"start": v(126.74, 42.39) * mm, "mid": v(112.75, 19.8) * mm, "end": v(90.96, 4.6) * mm});
            skArc(sketch, "E199.trimOffspring", {"start": v(122.17, 48.12) * mm, "mid": v(122.26, 49.77) * mm, "end": v(123, 51.24) * mm});
            skArc(sketch, "E200.trimOffspring", {"start": v(-130, -49.75) * mm, "mid": v(-129.99, -47.71) * mm, "end": v(-128.98, -45.94) * mm});
            skArc(sketch, "E201.trimOffspring", {"start": v(-126.74, -42.39) * mm, "mid": v(-112.75, -19.8) * mm, "end": v(-90.96, -4.6) * mm});
            skArc(sketch, "E202.trimOffspring", {"start": v(-121.6, -42.96) * mm, "mid": v(-102.6, -17.28) * mm, "end": v(-73.17, -4.8) * mm});
            skArc(sketch, "E203.trimOffspring", {"start": v(-56, -125.08) * mm, "mid": v(-80.08, -123.85) * mm, "end": v(-101.79, -113.35) * mm});
            skArc(sketch, "E204.trimOffspring", {"start": v(-53.95, -129.81) * mm, "mid": v(-111.5, -111.5) * mm, "end": v(-129.81, -53.95) * mm});
            skArc(sketch, "E205.trimOffspring", {"start": v(-49.75, -130) * mm, "mid": v(-47.71, -129.99) * mm, "end": v(-45.94, -128.98) * mm});
            skArc(sketch, "E206.trimOffspring", {"start": v(42.39, -126.74) * mm, "mid": v(19.8, -112.75) * mm, "end": v(4.6, -90.96) * mm});
            skArc(sketch, "E207.trimOffspring", {"start": v(42.96, -121.6) * mm, "mid": v(17.28, -102.6) * mm, "end": v(4.8, -73.17) * mm});
            skArc(sketch, "E208.trimOffspring", {"start": v(48.12, -122.17) * mm, "mid": v(49.77, -122.26) * mm, "end": v(51.24, -123) * mm});
            skArc(sketch, "E209.trimOffspring", {"start": v(130, -49.75) * mm, "mid": v(129.99, -47.71) * mm, "end": v(128.98, -45.94) * mm});
            skArc(sketch, "E210.trimOffspring", {"start": v(129.81, -53.95) * mm, "mid": v(111.5, -111.5) * mm, "end": v(53.95, -129.81) * mm});
            skPoint(sketch, "E211.visualSharp", {"position": v(-45.04, 127.65) * mm});
            skArc(sketch, "E211.filletArc", {"start": v(-45.94, 128.98) * mm, "mid": v(-44.28, 127.67) * mm, "end": v(-42.39, 126.74) * mm});
            skPoint(sketch, "E212.visualSharp", {"position": v(-46.45, 122.85) * mm});
            skArc(sketch, "E212.filletArc", {"start": v(-42.96, 121.6) * mm, "mid": v(-45.5, 122.23) * mm, "end": v(-48.12, 122.17) * mm});
            skPoint(sketch, "E213.visualSharp", {"position": v(-51.2, 129.28) * mm});
            skArc(sketch, "E213.filletArc", {"start": v(-53.95, 129.81) * mm, "mid": v(-51.84, 129.68) * mm, "end": v(-49.75, 130) * mm});
            skPoint(sketch, "E214.visualSharp", {"position": v(-52.36, 124.42) * mm});
            skArc(sketch, "E214.filletArc", {"start": v(-51.24, 123) * mm, "mid": v(-53.48, 124.36) * mm, "end": v(-56, 125.08) * mm});
            skPoint(sketch, "E215.visualSharp", {"position": v(-124.42, 52.36) * mm});
            skArc(sketch, "E215.filletArc", {"start": v(-125.08, 56) * mm, "mid": v(-124.36, 53.48) * mm, "end": v(-123, 51.24) * mm});
            skPoint(sketch, "E216.visualSharp", {"position": v(-122.85, 46.45) * mm});
            skArc(sketch, "E216.filletArc", {"start": v(-122.17, 48.12) * mm, "mid": v(-122.23, 45.5) * mm, "end": v(-121.6, 42.96) * mm});
            skPoint(sketch, "E217.visualSharp", {"position": v(-129.28, 51.2) * mm});
            skArc(sketch, "E217.filletArc", {"start": v(-130, 49.75) * mm, "mid": v(-129.68, 51.84) * mm, "end": v(-129.81, 53.95) * mm});
            skPoint(sketch, "E218.visualSharp", {"position": v(-127.65, 45.04) * mm});
            skArc(sketch, "E218.filletArc", {"start": v(-126.74, 42.39) * mm, "mid": v(-127.67, 44.28) * mm, "end": v(-128.98, 45.94) * mm});
            skPoint(sketch, "E219.visualSharp", {"position": v(45.04, 127.65) * mm});
            skArc(sketch, "E219.filletArc", {"start": v(42.39, 126.74) * mm, "mid": v(44.28, 127.67) * mm, "end": v(45.94, 128.98) * mm});
            skPoint(sketch, "E220.visualSharp", {"position": v(51.2, 129.28) * mm});
            skArc(sketch, "E220.filletArc", {"start": v(49.75, 130) * mm, "mid": v(51.84, 129.68) * mm, "end": v(53.95, 129.81) * mm});
            skPoint(sketch, "E221.visualSharp", {"position": v(52.36, 124.42) * mm});
            skArc(sketch, "E221.filletArc", {"start": v(56, 125.08) * mm, "mid": v(53.48, 124.36) * mm, "end": v(51.24, 123) * mm});
            skPoint(sketch, "E222.visualSharp", {"position": v(46.45, 122.85) * mm});
            skArc(sketch, "E222.filletArc", {"start": v(48.12, 122.17) * mm, "mid": v(45.5, 122.23) * mm, "end": v(42.96, 121.6) * mm});
            skPoint(sketch, "E223.visualSharp", {"position": v(124.42, 52.36) * mm});
            skArc(sketch, "E223.filletArc", {"start": v(123, 51.24) * mm, "mid": v(124.36, 53.48) * mm, "end": v(125.08, 56) * mm});
            skPoint(sketch, "E224.visualSharp", {"position": v(122.85, 46.45) * mm});
            skArc(sketch, "E224.filletArc", {"start": v(121.6, 42.96) * mm, "mid": v(122.23, 45.5) * mm, "end": v(122.17, 48.12) * mm});
            skPoint(sketch, "E225.visualSharp", {"position": v(127.65, 45.04) * mm});
            skArc(sketch, "E225.filletArc", {"start": v(128.98, 45.94) * mm, "mid": v(127.67, 44.28) * mm, "end": v(126.74, 42.39) * mm});
            skPoint(sketch, "E226.visualSharp", {"position": v(129.28, 51.2) * mm});
            skArc(sketch, "E226.filletArc", {"start": v(129.81, 53.95) * mm, "mid": v(129.68, 51.84) * mm, "end": v(130, 49.75) * mm});
            skArc(sketch, "E227.trimOffspring", {"start": v(125.08, -56) * mm, "mid": v(123.85, -80.08) * mm, "end": v(113.35, -101.79) * mm});
            skPoint(sketch, "E228.visualSharp", {"position": v(127.65, -45.04) * mm});
            skArc(sketch, "E228.filletArc", {"start": v(126.74, -42.39) * mm, "mid": v(127.67, -44.28) * mm, "end": v(128.98, -45.94) * mm});
            skPoint(sketch, "E229.visualSharp", {"position": v(129.28, -51.2) * mm});
            skArc(sketch, "E229.filletArc", {"start": v(130, -49.75) * mm, "mid": v(129.68, -51.84) * mm, "end": v(129.81, -53.95) * mm});
            skPoint(sketch, "E230.visualSharp", {"position": v(124.42, -52.36) * mm});
            skArc(sketch, "E230.filletArc", {"start": v(125.08, -56) * mm, "mid": v(124.36, -53.48) * mm, "end": v(123, -51.24) * mm});
            skPoint(sketch, "E231.visualSharp", {"position": v(122.85, -46.45) * mm});
            skArc(sketch, "E231.filletArc", {"start": v(122.17, -48.12) * mm, "mid": v(122.23, -45.5) * mm, "end": v(121.6, -42.96) * mm});
            skPoint(sketch, "E232.visualSharp", {"position": v(52.36, -124.42) * mm});
            skArc(sketch, "E232.filletArc", {"start": v(51.24, -123) * mm, "mid": v(53.48, -124.36) * mm, "end": v(56, -125.08) * mm});
            skPoint(sketch, "E233.visualSharp", {"position": v(51.2, -129.28) * mm});
            skArc(sketch, "E233.filletArc", {"start": v(53.95, -129.81) * mm, "mid": v(51.84, -129.68) * mm, "end": v(49.75, -130) * mm});
            skPoint(sketch, "E234.visualSharp", {"position": v(45.04, -127.65) * mm});
            skArc(sketch, "E234.filletArc", {"start": v(45.94, -128.98) * mm, "mid": v(44.28, -127.67) * mm, "end": v(42.39, -126.74) * mm});
            skPoint(sketch, "E235.visualSharp", {"position": v(46.45, -122.85) * mm});
            skArc(sketch, "E235.filletArc", {"start": v(42.96, -121.6) * mm, "mid": v(45.5, -122.23) * mm, "end": v(48.12, -122.17) * mm});
            skPoint(sketch, "E236.visualSharp", {"position": v(-46.45, -122.85) * mm});
            skArc(sketch, "E236.filletArc", {"start": v(-48.12, -122.17) * mm, "mid": v(-45.5, -122.23) * mm, "end": v(-42.96, -121.6) * mm});
            skPoint(sketch, "E237.visualSharp", {"position": v(-45.04, -127.65) * mm});
            skArc(sketch, "E237.filletArc", {"start": v(-42.39, -126.74) * mm, "mid": v(-44.28, -127.67) * mm, "end": v(-45.94, -128.98) * mm});
            skPoint(sketch, "E238.visualSharp", {"position": v(-51.2, -129.28) * mm});
            skArc(sketch, "E238.filletArc", {"start": v(-49.75, -130) * mm, "mid": v(-51.84, -129.68) * mm, "end": v(-53.95, -129.81) * mm});
            skPoint(sketch, "E239.visualSharp", {"position": v(-52.36, -124.42) * mm});
            skArc(sketch, "E239.filletArc", {"start": v(-56, -125.08) * mm, "mid": v(-53.48, -124.36) * mm, "end": v(-51.24, -123) * mm});
            skPoint(sketch, "E240.visualSharp", {"position": v(-124.42, -52.36) * mm});
            skArc(sketch, "E240.filletArc", {"start": v(-123, -51.24) * mm, "mid": v(-124.36, -53.48) * mm, "end": v(-125.08, -56) * mm});
            skPoint(sketch, "E241.visualSharp", {"position": v(-122.85, -46.45) * mm});
            skArc(sketch, "E241.filletArc", {"start": v(-121.6, -42.96) * mm, "mid": v(-122.23, -45.5) * mm, "end": v(-122.17, -48.12) * mm});
            skPoint(sketch, "E242.visualSharp", {"position": v(-129.28, -51.2) * mm});
            skArc(sketch, "E242.filletArc", {"start": v(-129.81, -53.95) * mm, "mid": v(-129.68, -51.84) * mm, "end": v(-130, -49.75) * mm});
            skPoint(sketch, "E243.visualSharp", {"position": v(-127.65, -45.04) * mm});
            skArc(sketch, "E243.filletArc", {"start": v(-128.98, -45.94) * mm, "mid": v(-127.67, -44.28) * mm, "end": v(-126.74, -42.39) * mm});
            skCircle(sketch, "E244", {"center": v(-65, 65) * mm, "radius": 63.25 * mm, "construction": true});
            skCircle(sketch, "E245", {"center": v(65, 65) * mm, "radius": 63.25 * mm, "construction": true});
            skCircle(sketch, "E246", {"center": v(-65, -65) * mm, "radius": 63.25 * mm, "construction": true});
            skPoint(sketch, "E247.second.point", {"position": v(-109.7, 103.75) * mm});
            skPoint(sketch, "E247.third.point", {"position": v(-103.7, 108.66) * mm});
            skPoint(sketch, "E248.second.point", {"position": v(103.75, 109.7) * mm});
            skPoint(sketch, "E248.third.point", {"position": v(109.03, 103.75) * mm});
            skPoint(sketch, "E248.third.point.positionSnap0", {"position": v(109.7, 103.75) * mm});
            skPoint(sketch, "E249.second.point", {"position": v(109.7, -103.75) * mm});
            skPoint(sketch, "E249.third.point", {"position": v(103.76, -109.16) * mm});
            skPoint(sketch, "E250.second.point", {"position": v(-109.7, -103.75) * mm});
            skPoint(sketch, "E250.third.point", {"position": v(-103.75, -109.03) * mm});
            skPoint(sketch, "E250.third.point.positionSnap0", {"position": v(-103.75, -109.7) * mm});
            skCircle(sketch, "E251", {"center": v(-108.3, 108.15) * mm, "radius": 1.55 * mm});
            skCircle(sketch, "E252", {"center": v(-48.74, 126.12) * mm, "radius": 1.55 * mm});
            skCircle(sketch, "E253", {"center": v(-126.12, 48.74) * mm, "radius": 1.55 * mm});
            skCircle(sketch, "E254", {"center": v(-126.12, -48.74) * mm, "radius": 1.55 * mm});
            skCircle(sketch, "E255", {"center": v(-108.3, -108.15) * mm, "radius": 1.55 * mm});
            skCircle(sketch, "E256", {"center": v(-48.74, -126.12) * mm, "radius": 1.55 * mm});
            skCircle(sketch, "E257", {"center": v(48.74, -126.12) * mm, "radius": 1.55 * mm});
            skCircle(sketch, "E258", {"center": v(108.28, -108.16) * mm, "radius": 1.55 * mm});
            skCircle(sketch, "E259", {"center": v(126.12, -48.74) * mm, "radius": 1.55 * mm});
            skCircle(sketch, "E260", {"center": v(126.12, 48.74) * mm, "radius": 1.55 * mm});
            skCircle(sketch, "E261", {"center": v(108.15, 108.3) * mm, "radius": 1.55 * mm});
            skCircle(sketch, "E262", {"center": v(48.74, 126.12) * mm, "radius": 1.55 * mm});
            skCircle(sketch, "E263", {"center": v(0, 79.89) * mm, "radius": 1.55 * mm});
            skCircle(sketch, "E264", {"center": v(-79.89, 0) * mm, "radius": 1.55 * mm});
            skCircle(sketch, "E265.MirrorC", {"center": v(0, -79.89) * mm, "radius": 1.55 * mm});
            skCircle(sketch, "E266.MirrorC", {"center": v(79.89, 0) * mm, "radius": 1.55 * mm});
            skPoint(sketch, "E267", {"position": v(-38, 0) * mm});
            skPoint(sketch, "E268", {"position": v(-30.1, 12.25) * mm});
            skPoint(sketch, "E269", {"position": v(-29.62, -12.57) * mm});
            skFitSpline(sketch, "E270", {"points": [v(-30.1, 12.25) * mm, v(-38, 0) * mm, v(-29.62, -12.57) * mm], "startDerivative": vector(-28.95, -24.66) * mm, "endDerivative": vector(29.75, -24.97) * mm});
            skFitSpline(sketch, "E271", {"points": [v(12.63, 29.53) * mm, v(0, 38) * mm, v(-12.54, 29.66) * mm], "startDerivative": vector(-25.22, 22.7) * mm, "endDerivative": vector(-25.13, -22.48) * mm});
            skArc(sketch, "E272.filletArc", {"start": v(-15.95, 31.77) * mm, "mid": v(-12.77, 30.92) * mm, "end": v(-9.75, 32.23) * mm});
            skArc(sketch, "E273.filletArc", {"start": v(9.88, 32.08) * mm, "mid": v(12.86, 30.76) * mm, "end": v(16.03, 31.56) * mm});
            skArc(sketch, "E274.filletArc", {"start": v(-33.1, 9.47) * mm, "mid": v(-31.7, 12.66) * mm, "end": v(-32.72, 16) * mm});
            skArc(sketch, "E275.filletArc", {"start": v(-31.96, -16.3) * mm, "mid": v(-31.1, -13) * mm, "end": v(-32.55, -9.91) * mm});
            skCircle(sketch, "E276", {"center": v(-32.05, 0) * mm, "radius": 1.55 * mm});
            skCircle(sketch, "E277", {"center": v(0, 32.05) * mm, "radius": 1.55 * mm});
            skCircle(sketch, "E278.MirrorC", {"center": v(32.05, 0) * mm, "radius": 1.55 * mm});
            skPoint(sketch, "E279.orphan", {"position": v(33.1, 9.47) * mm});
            skPoint(sketch, "E280.orphan", {"position": v(32.72, 16) * mm});
            skPoint(sketch, "E281.MirrorCS.end.orphan", {"position": v(32.55, -9.91) * mm});
            skPoint(sketch, "E282.MirrorCS.start.orphan", {"position": v(31.96, -16.3) * mm});
            skCircle(sketch, "E283", {"center": v(65, -65) * mm, "radius": 63.3 * mm, "construction": true});
            skFitSpline(sketch, "E284", {"points": [v(29.94, 12.36) * mm, v(38, 0) * mm, v(29.52, -12.58) * mm], "startDerivative": vector(27.42, -24.86) * mm, "endDerivative": vector(-28.13, -25.02) * mm});
            skArc(sketch, "E285.filletArc", {"start": v(32.39, 16.02) * mm, "mid": v(31.43, 12.73) * mm, "end": v(32.82, 9.59) * mm});
            skArc(sketch, "E286.filletArc", {"start": v(32.35, -9.92) * mm, "mid": v(30.92, -12.97) * mm, "end": v(31.75, -16.24) * mm});
            skFitSpline(sketch, "E287", {"points": [v(12.32, -29.91) * mm, v(0, -38) * mm, v(-12.48, -29.76) * mm], "startDerivative": vector(-24.7, -18.64) * mm, "endDerivative": vector(-24.9, 18.9) * mm});
            skArc(sketch, "E288.filletArc", {"start": v(15.59, -32.07) * mm, "mid": v(12.42, -31.14) * mm, "end": v(9.36, -32.38) * mm});
            skArc(sketch, "E289.filletArc", {"start": v(-9.57, -32.2) * mm, "mid": v(-12.6, -30.95) * mm, "end": v(-15.74, -31.84) * mm});
            skCircle(sketch, "E290.MirrorC", {"center": v(0, -32.05) * mm, "radius": 1.55 * mm});
            skSolve(sketch);
        }
        {
            var Q0;
            {var subQ3=sQuery(id+"F0.wireOp",EDGE,"E10");Q0=makeQuery(id+"F0.imprint","IMPRINT",FACE,{"disambiguationData":[TD([[makeQuery(id+"F0.imprint","IMPRINT",EDGE,{"derivedFrom":subQ3}),1.0]])]});}
            var Q1;
            {var subQ0=sQuery(id+"F0.wireOp",EDGE,"E21.0.startCap");Q1=makeQuery(id+"F0.imprint","IMPRINT",FACE,{"disambiguationData":[TD([[makeQuery(id+"F0.imprint","IMPRINT",EDGE,{"derivedFrom":subQ0}),1.0]])]});}
            var Q2;
            {var subQ3=sQuery(id+"F0.wireOp",EDGE,"E21.0.endCap");Q2=makeQuery(id+"F0.imprint","IMPRINT",FACE,{"disambiguationData":[TD([[makeQuery(id+"F0.imprint","IMPRINT",EDGE,{"derivedFrom":subQ3}),1.0]])]});}
            var Q3;
            {var subQ3=sQuery(id+"F0.wireOp",EDGE,"E21.0.endCap");Q3=makeQuery(id+"F0.imprint","IMPRINT",FACE,{"disambiguationData":[TD([[makeQuery(id+"F0.imprint","IMPRINT",EDGE,{"derivedFrom":subQ3}),-1.0]])]});}
            var Q4;
            {var subQ3=sQuery(id+"F0.wireOp",EDGE,"E21.0.startCap");Q4=makeQuery(id+"F0.imprint","IMPRINT",FACE,{"disambiguationData":[TD([[makeQuery(id+"F0.imprint","IMPRINT",EDGE,{"derivedFrom":subQ3}),-1.0]])]});}
            var Q5;
            {var subQ3=sQuery(id+"F0.wireOp",EDGE,"E22.0.startCap");Q5=makeQuery(id+"F0.imprint","IMPRINT",FACE,{"disambiguationData":[TD([[makeQuery(id+"F0.imprint","IMPRINT",EDGE,{"derivedFrom":subQ3}),-1.0]])]});}
            var Q6;
            {var subQ1=sQuery(id+"F0.wireOp",EDGE,"E22.1.endCap");Q6=makeQuery(id+"F0.imprint","IMPRINT",FACE,{"disambiguationData":[TD([[makeQuery(id+"F0.imprint","IMPRINT",EDGE,{"derivedFrom":subQ1}),1.0]])]});}
            var Q7;
            {var subQ1=sQuery(id+"F0.wireOp",EDGE,"E22.1.endCap");Q7=makeQuery(id+"F0.imprint","IMPRINT",FACE,{"disambiguationData":[TD([[makeQuery(id+"F0.imprint","IMPRINT",EDGE,{"derivedFrom":subQ1}),-1.0]])]});}
            var Q8;
            {var subQ4=sQuery(id+"F0.wireOp",EDGE,"E22.0.startCap");Q8=makeQuery(id+"F0.imprint","IMPRINT",FACE,{"disambiguationData":[TD([[makeQuery(id+"F0.imprint","IMPRINT",EDGE,{"derivedFrom":subQ4}),1.0]])]});}
            var Q9;
            {var subQ1=sQuery(id+"F0.wireOp",EDGE,"E9.rect.left");var subQ8=sQuery(id+"F0.wireOp",EDGE,"E9.rect.bottom");var subQ9=makeQuery(id+"F0.imprint","INTERSECT",VERTEX,{"derivedFrom":[subQ8,subQ1]});Q9=makeQuery(id+"F0.imprint","IMPRINT",FACE,{"disambiguationData":[TD([[makeQuery(id+"F0.imprint","IMPRINT",EDGE,{"disambiguationData":[TD([[subQ9,-1.0]])],"derivedFrom":subQ8}),-1.0]])]});}
            extrude(context, id + "F1", {"entities" : qUnion([Q0, Q1, Q2, Q3, Q4, Q5, Q6, Q7, Q8, Q9]), "depth" : 3 * mm});
        }
    });
